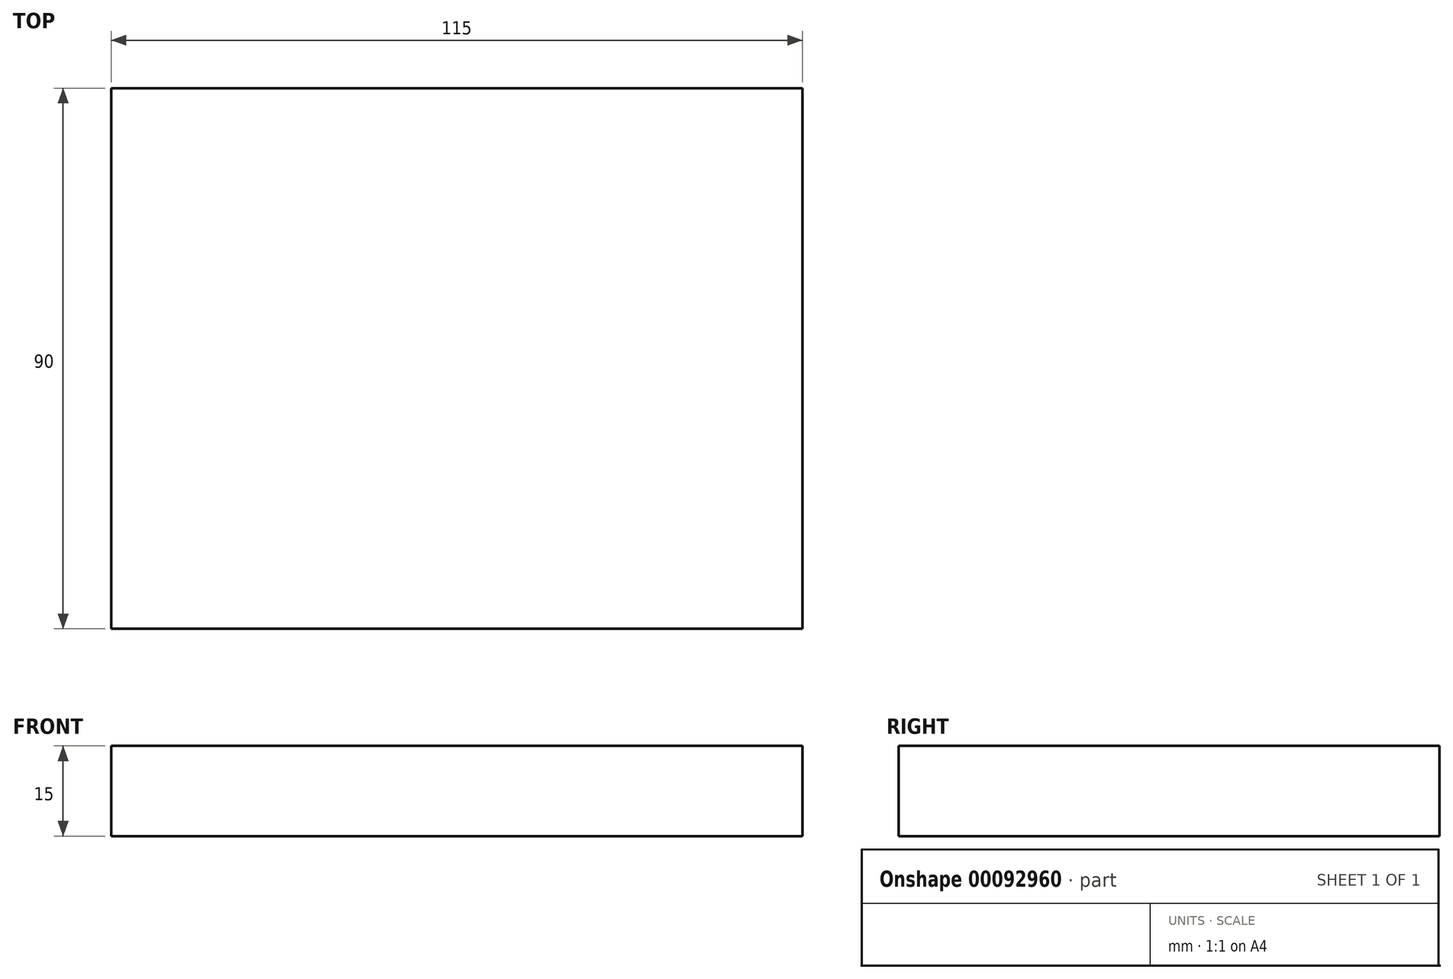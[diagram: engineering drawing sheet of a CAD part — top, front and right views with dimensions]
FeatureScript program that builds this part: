
annotation { "Feature Type Name" : "Feature", "Feature Type Description" : "" }
export const myFeature = defineFeature(function(context is Context, id is Id, definition is map)
    precondition{}
    {
        {
            var Q0;
            Q0=qCreatedBy(makeId("Top.planeOp"),FACE);
            var sketch = newSketch(context, id + "F0", { "sketchPlane" : qUnion([Q0])});
            skLineSegment(sketch, "E0.bottom", {"start": v(57.5, 45) * mm, "end": v(-57.5, 45) * mm});
            skLineSegment(sketch, "E0.top", {"start": v(57.5, -45) * mm, "end": v(-57.5, -45) * mm});
            skLineSegment(sketch, "E0.left", {"start": v(57.5, 45) * mm, "end": v(57.5, -45) * mm});
            skLineSegment(sketch, "E0.right", {"start": v(-57.5, 45) * mm, "end": v(-57.5, -45) * mm});
            skPoint(sketch, "E0.middle", {"position": v(0, 0) * mm});
            skSolve(sketch);
        }
        {
            var Q0;
            Q0 = qSketchRegion(id + "F0", true);
            var Q1;
            Q1=makeQuery(id+"F0.imprint","IMPRINT",FACE,{"disambiguationData":[TD([[makeQuery(id+"F0.imprint","IMPRINT",EDGE,{"derivedFrom":sQuery(id+"F0.wireOp",EDGE,"E0.bottom")}),1.0]])]});
            extrude(context, id + "F1", {"entities" : qUnion([Q0, Q1]), "depth" : 15 * mm});
        }
    });
